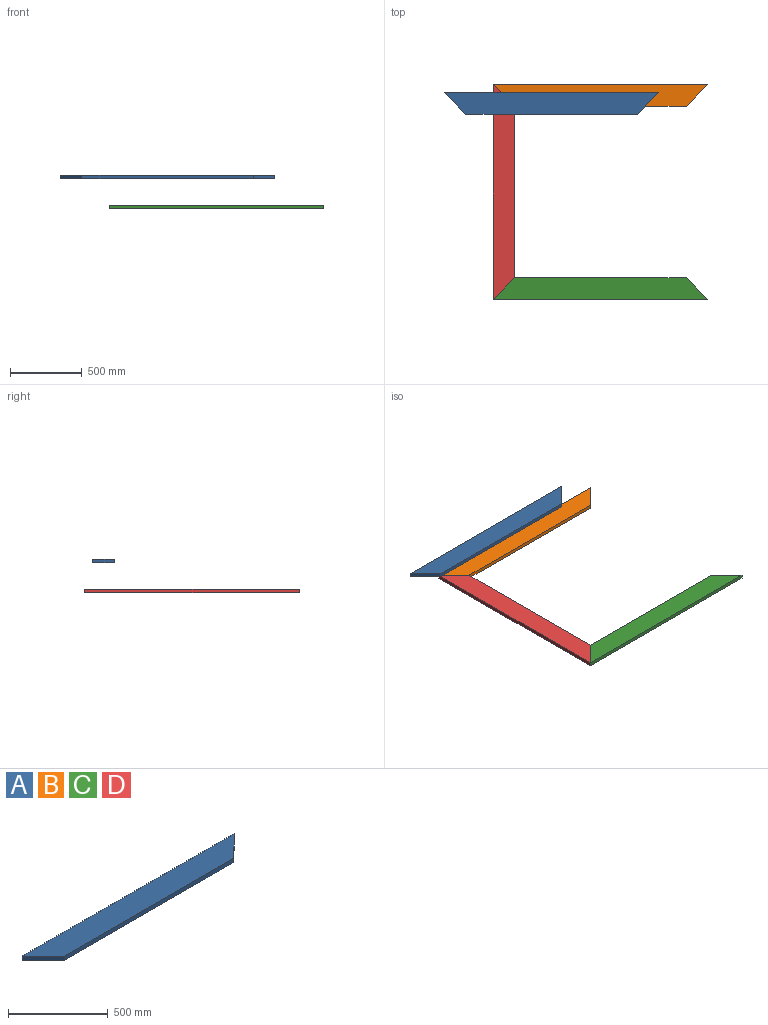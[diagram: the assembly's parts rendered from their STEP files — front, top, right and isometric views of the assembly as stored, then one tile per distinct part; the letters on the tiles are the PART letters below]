
ASSEMBLY  parts=4 mates=2
PART A: 6 faces, bbox 1500x150x25 mm
  f0: plane 1500x25mm, normal (0,1,0), area 37500mm2, adj f1,f3,f4,f5
  f1: plane 150x150mm, normal (-0.71,-0.71,0), area 5303.3mm2, adj f0,f2,f4,f5
  f2: plane 1200x25mm, normal (0,-1,0), area 30000mm2, adj f1,f3,f4,f5
  f3: plane 150x150mm, normal (0.71,-0.71,0), area 5303.3mm2, adj f0,f2,f4,f5
  f4: plane 1500x150mm, normal (0,0,1), area 202500mm2, adj f0,f1,f2,f3
  f5: plane 1500x150mm, normal (0,0,-1), area 202500mm2, adj f0,f1,f2,f3
PART B: same geometry as A
PART C: same geometry as A
PART D: same geometry as A
PLACE A t=(-235.38,-162.01,109.17)mm
PLACE B t=(103.92,-106.01,-100.68)mm
PLACE C rot(axis=(0,0,-1),180deg) t=(-7.71,-1306.01,-100.68)mm
PLACE D rot(axis=(0,0,1),90deg) t=(-551.89,-650.2,-100.68)mm
MATE fastened D.f1 <-> C.f3  axis (0.71,-0.71,0) through (-551.89,-1306.01,-88.18)mm
MATE fastened D.f3 <-> B.f1  axis (0.71,0.71,0) through (-551.89,-106.01,-88.18)mm
